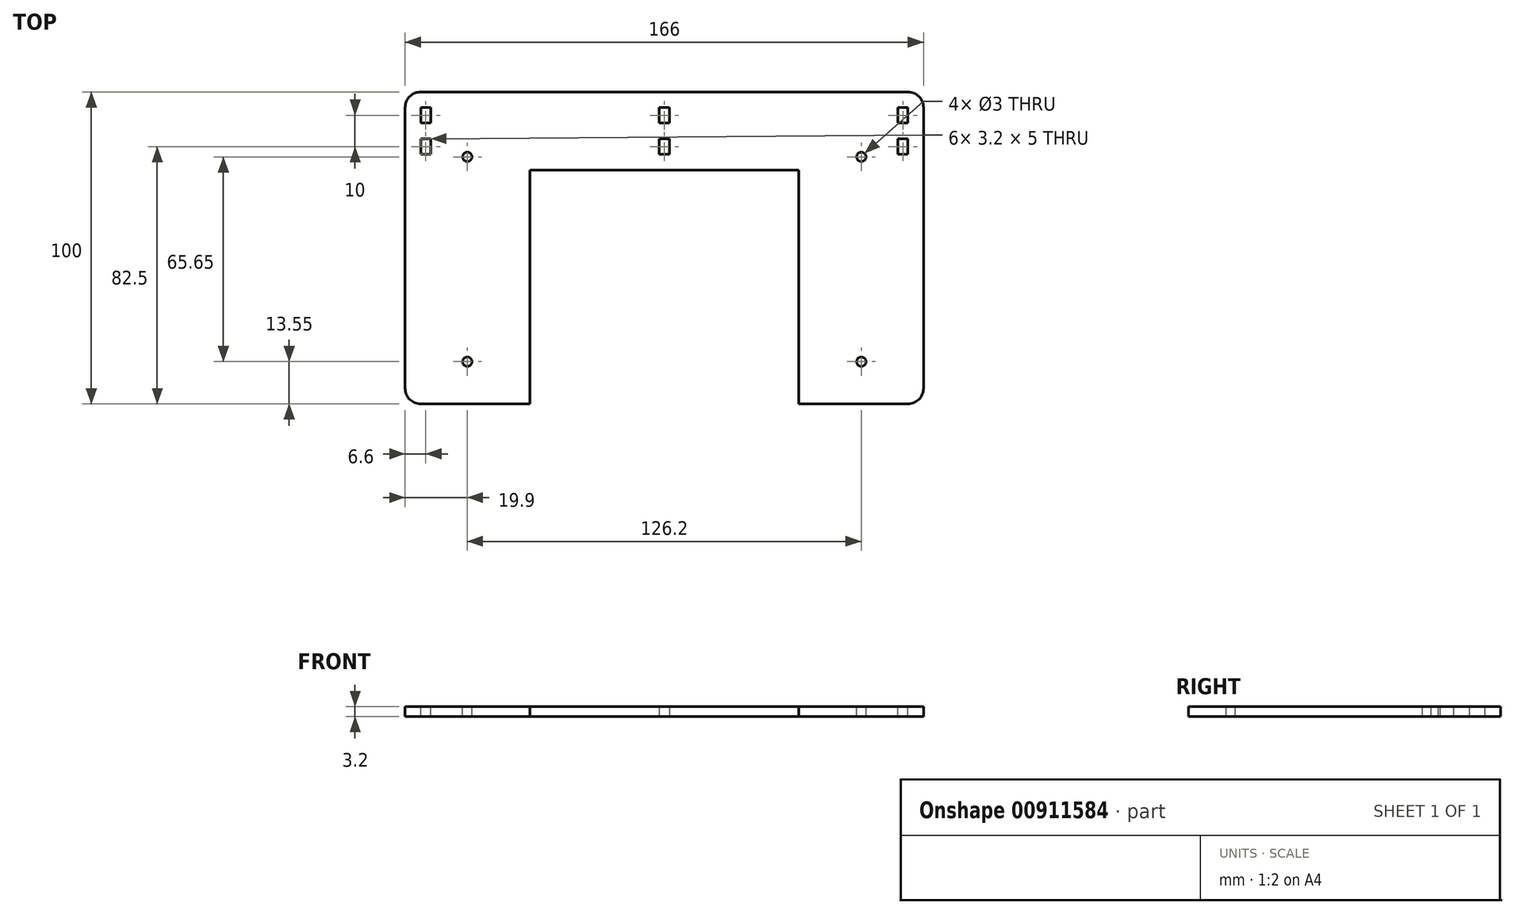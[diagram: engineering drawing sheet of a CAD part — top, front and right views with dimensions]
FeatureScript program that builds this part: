
annotation { "Feature Type Name" : "Feature", "Feature Type Description" : "" }
export const myFeature = defineFeature(function(context is Context, id is Id, definition is map)
    precondition{}
    {
        {
            var Q0;
            Q0=qCreatedBy(makeId("Top.planeOp"),FACE);
            var sketch = newSketch(context, id + "F0", { "sketchPlane" : qUnion([Q0])});
            skLineSegment(sketch, "E0.bottom", {"start": v(83, 50) * mm, "end": v(-83, 50) * mm});
            skLineSegment(sketch, "E0.top", {"start": v(83, -50) * mm, "end": v(-83, -50) * mm});
            skLineSegment(sketch, "E0.left", {"start": v(83, 50) * mm, "end": v(83, -50) * mm});
            skLineSegment(sketch, "E0.right", {"start": v(-83, 50) * mm, "end": v(-83, -50) * mm});
            skPoint(sketch, "E0.middle", {"position": v(0, 0) * mm});
            skSolve(sketch);
        }
        {
            var Q0;
            Q0=makeQuery(id+"F0.imprint","IMPRINT",FACE,{"disambiguationData":[TD([[makeQuery(id+"F0.imprint","IMPRINT",EDGE,{"derivedFrom":sQuery(id+"F0.wireOp",EDGE,"E0.bottom")}),1.0]])]});
            extrude(context, id + "F1", {"entities" : qUnion([Q0]), "depth" : 3.2 * mm, "offsetDistance" : 25 * mm});
        }
        {
            var Q0;
            Q0=makeQuery(id+"F1.opExtrude","SWEPT_EDGE",EDGE,{"disambiguationData":[OSD([sQuery(id+"F0.wireOp",EDGE,"E0.bottom"),sQuery(id+"F0.wireOp",EDGE,"E0.left")])]});
            var Q1;
            Q1=makeQuery(id+"F1.opExtrude","SWEPT_EDGE",EDGE,{"disambiguationData":[OSD([sQuery(id+"F0.wireOp",EDGE,"E0.top"),sQuery(id+"F0.wireOp",EDGE,"E0.left")])]});
            var Q2;
            Q2=makeQuery(id+"F1.opExtrude","SWEPT_EDGE",EDGE,{"disambiguationData":[OSD([sQuery(id+"F0.wireOp",EDGE,"E0.top"),sQuery(id+"F0.wireOp",EDGE,"E0.right")])]});
            var Q3;
            Q3=makeQuery(id+"F1.opExtrude","SWEPT_EDGE",EDGE,{"disambiguationData":[OSD([sQuery(id+"F0.wireOp",EDGE,"E0.bottom"),sQuery(id+"F0.wireOp",EDGE,"E0.right")])]});
            fillet(context, id + "F2", {"entities" : qUnion([Q0, Q1, Q2, Q3]), "radius" : 5 * mm, "tangentPropagation" : true, "allowEdgeOverflow" : false});
        }
        {
            var Q0;
            Q0=makeQuery(id+"F1.opExtrude","CAP_FACE",FACE,{"disambiguationData":[OSD([sQuery(id+"F0.wireOp",EDGE,"E0.bottom"),sQuery(id+"F0.wireOp",EDGE,"E0.top"),sQuery(id+"F0.wireOp",EDGE,"E0.left"),sQuery(id+"F0.wireOp",EDGE,"E0.right")])],"isStart":false});
            var sketch = newSketch(context, id + "F3", { "sketchPlane" : qUnion([Q0])});
            skLineSegment(sketch, "E1", {"start": v(0, 50) * mm, "end": v(0, 29.2) * mm, "construction": true});
            skLineSegment(sketch, "E2", {"start": v(0, 29.2) * mm, "end": v(63.1, 29.2) * mm, "construction": true});
            skCircle(sketch, "E3", {"center": v(63.1, 29.2) * mm, "radius": 1.5 * mm});
            skCircle(sketch, "E4.MirrorC", {"center": v(-63.1, 29.2) * mm, "radius": 1.5 * mm});
            skLineSegment(sketch, "E5", {"start": v(0, 29.2) * mm, "end": v(0, -3.62) * mm, "construction": true});
            skLineSegment(sketch, "E6", {"start": v(0, -3.62) * mm, "end": v(38.49, -3.62) * mm, "construction": true});
            skCircle(sketch, "E7.MirrorC", {"center": v(-63.1, -36.45) * mm, "radius": 1.5 * mm});
            skCircle(sketch, "E8.MirrorC", {"center": v(63.1, -36.45) * mm, "radius": 1.5 * mm});
            skSolve(sketch);
        }
        {
            var Q0;
            Q0 = qSketchRegion(id + "F3", true);
            extrude(context, id + "F4", {"entities" : qUnion([Q0]), "operationType" : NewBodyOperationType.REMOVE, "oppositeDirection" : true, "depth" : 25 * mm, "offsetDistance" : 25 * mm});
        }
        {
            var Q0;
            Q0=makeQuery(id+"F1.opExtrude","CAP_FACE",FACE,{"disambiguationData":[OSD([sQuery(id+"F0.wireOp",EDGE,"E0.bottom"),sQuery(id+"F0.wireOp",EDGE,"E0.top"),sQuery(id+"F0.wireOp",EDGE,"E0.left"),sQuery(id+"F0.wireOp",EDGE,"E0.right")])],"isStart":false});
            var sketch = newSketch(context, id + "F5", { "sketchPlane" : qUnion([Q0])});
            skLineSegment(sketch, "E9", {"start": v(-63.1, -36.45) * mm, "end": v(-63.1, 29.2) * mm, "construction": true});
            skLineSegment(sketch, "E10", {"start": v(-63.1, 29.2) * mm, "end": v(63.1, 29.2) * mm, "construction": true});
            skLineSegment(sketch, "E11", {"start": v(63.1, 29.2) * mm, "end": v(63.1, -50) * mm, "construction": true});
            skLineSegment(sketch, "E12", {"start": v(-63.1, -36.45) * mm, "end": v(-63.1, -50) * mm, "construction": true});
            skLineSegment(sketch, "E13.0", {"start": v(43.1, 9.2) * mm, "end": v(43.1, -50) * mm, "construction": true});
            skLineSegment(sketch, "E13.1", {"start": v(-43.1, 9.2) * mm, "end": v(43.1, 9.2) * mm, "construction": true});
            skLineSegment(sketch, "E13.2", {"start": v(-43.1, -36.45) * mm, "end": v(-43.1, 9.2) * mm, "construction": true});
            skLineSegment(sketch, "E13.3", {"start": v(-43.1, -36.45) * mm, "end": v(-43.1, -50) * mm, "construction": true});
            skLineSegment(sketch, "E14", {"start": v(0, 50) * mm, "end": v(0, 30) * mm});
            skLineSegment(sketch, "E15", {"start": v(-43.1, -50) * mm, "end": v(-43.1, 30) * mm});
            skLineSegment(sketch, "E16", {"start": v(-43.1, 30) * mm, "end": v(0, 30) * mm});
            skLineSegment(sketch, "E17.MirrorCS", {"start": v(43.1, 30) * mm, "end": v(0, 30) * mm});
            skLineSegment(sketch, "E18.MirrorCS", {"start": v(43.1, -50) * mm, "end": v(43.1, 30) * mm});
            skLineSegment(sketch, "E19", {"start": v(-43.1, -50) * mm, "end": v(43.1, -50) * mm});
            skSolve(sketch);
        }
        {
            var Q0;
            Q0=makeQuery(id+"F5.imprint","IMPRINT",FACE,{"disambiguationData":[TD([[makeQuery(id+"F5.imprint","IMPRINT",EDGE,{"derivedFrom":sQuery(id+"F5.wireOp",EDGE,"E15")}),-1.0]])]});
            extrude(context, id + "F6", {"entities" : qUnion([Q0]), "operationType" : NewBodyOperationType.REMOVE, "oppositeDirection" : true, "depth" : 25 * mm, "offsetDistance" : 25 * mm});
        }
        {
            var Q0;
            Q0=makeQuery(id+"F1.opExtrude","CAP_FACE",FACE,{"disambiguationData":[OSD([sQuery(id+"F0.wireOp",EDGE,"E0.bottom"),sQuery(id+"F0.wireOp",EDGE,"E0.top"),sQuery(id+"F0.wireOp",EDGE,"E0.left"),sQuery(id+"F0.wireOp",EDGE,"E0.right")])],"isStart":false});
            var sketch = newSketch(context, id + "F7", { "sketchPlane" : qUnion([Q0])});
            skLineSegment(sketch, "E20", {"start": v(-78, 50) * mm, "end": v(-78, 45) * mm, "construction": true});
            skLineSegment(sketch, "E21", {"start": v(-78, 45) * mm, "end": v(-78, 25) * mm, "construction": true});
            skLineSegment(sketch, "E22.bottom", {"start": v(-78, 45) * mm, "end": v(-74.8, 45) * mm});
            skLineSegment(sketch, "E22.top", {"start": v(-78, 40) * mm, "end": v(-74.8, 40) * mm});
            skLineSegment(sketch, "E22.left", {"start": v(-78, 45) * mm, "end": v(-78, 40) * mm});
            skLineSegment(sketch, "E22.right", {"start": v(-74.8, 45) * mm, "end": v(-74.8, 40) * mm});
            skLineSegment(sketch, "E23", {"start": v(-78, 40) * mm, "end": v(-78, 35) * mm, "construction": true});
            skLineSegment(sketch, "E24.bottom", {"start": v(-78, 35) * mm, "end": v(-74.8, 35) * mm});
            skLineSegment(sketch, "E24.top", {"start": v(-78, 30) * mm, "end": v(-74.8, 30) * mm});
            skLineSegment(sketch, "E24.left", {"start": v(-78, 35) * mm, "end": v(-78, 30) * mm});
            skLineSegment(sketch, "E24.right", {"start": v(-74.8, 35) * mm, "end": v(-74.8, 30) * mm});
            skLineSegment(sketch, "E25", {"start": v(0, 30) * mm, "end": v(0, 37.4) * mm, "construction": true});
            skLineSegment(sketch, "E26.MirrorCS", {"start": v(78, 50) * mm, "end": v(78, 45) * mm, "construction": true});
            skLineSegment(sketch, "E27.MirrorCS", {"start": v(78, 35) * mm, "end": v(74.8, 35) * mm});
            skLineSegment(sketch, "E28.MirrorCS", {"start": v(78, 30) * mm, "end": v(74.8, 30) * mm});
            skLineSegment(sketch, "E29.MirrorCS", {"start": v(78, 45) * mm, "end": v(74.8, 45) * mm});
            skLineSegment(sketch, "E30.MirrorCS", {"start": v(78, 40) * mm, "end": v(74.8, 40) * mm});
            skLineSegment(sketch, "E31.MirrorCS", {"start": v(78, 45) * mm, "end": v(78, 40) * mm});
            skLineSegment(sketch, "E32.MirrorCS", {"start": v(78, 40) * mm, "end": v(78, 35) * mm, "construction": true});
            skLineSegment(sketch, "E33.MirrorCS", {"start": v(78, 35) * mm, "end": v(78, 30) * mm});
            skLineSegment(sketch, "E34.MirrorCS", {"start": v(74.8, 45) * mm, "end": v(74.8, 40) * mm});
            skLineSegment(sketch, "E35.MirrorCS", {"start": v(74.8, 35) * mm, "end": v(74.8, 30) * mm});
            skLineSegment(sketch, "E36.MirrorCS", {"start": v(78, 45) * mm, "end": v(78, 25) * mm, "construction": true});
            skSolve(sketch);
        }
        {
            var Q0;
            Q0 = qSketchRegion(id + "F7", true);
            extrude(context, id + "F8", {"entities" : qUnion([Q0]), "operationType" : NewBodyOperationType.REMOVE, "oppositeDirection" : true, "depth" : 25 * mm, "offsetDistance" : 25 * mm});
        }
        {
            var Q0;
            Q0=makeQuery(id+"F1.opExtrude","CAP_FACE",FACE,{"disambiguationData":[OSD([sQuery(id+"F0.wireOp",EDGE,"E0.bottom"),sQuery(id+"F0.wireOp",EDGE,"E0.top"),sQuery(id+"F0.wireOp",EDGE,"E0.left"),sQuery(id+"F0.wireOp",EDGE,"E0.right")])],"isStart":false});
            var sketch = newSketch(context, id + "F9", { "sketchPlane" : qUnion([Q0])});
            skLineSegment(sketch, "E37", {"start": v(-78, 30) * mm, "end": v(-78, 25) * mm, "construction": true});
            skLineSegment(sketch, "E38", {"start": v(-78, 25) * mm, "end": v(43.1, 25) * mm, "construction": true});
            skLineSegment(sketch, "E39.bottom", {"start": v(43.1, 25) * mm, "end": v(-43.1, 25) * mm});
            skLineSegment(sketch, "E39.top", {"start": v(43.1, 30) * mm, "end": v(-43.1, 30) * mm});
            skLineSegment(sketch, "E39.left", {"start": v(43.1, 25) * mm, "end": v(43.1, 30) * mm});
            skLineSegment(sketch, "E39.right", {"start": v(-43.1, 25) * mm, "end": v(-43.1, 30) * mm});
            skSolve(sketch);
        }
        {
            var Q0;
            Q0 = qSketchRegion(id + "F9", true);
            var Q1;
            Q1=makeQuery(id+"F1.opExtrude","CAP_FACE",FACE,{"disambiguationData":[OSD([sQuery(id+"F0.wireOp",EDGE,"E0.bottom"),sQuery(id+"F0.wireOp",EDGE,"E0.top"),sQuery(id+"F0.wireOp",EDGE,"E0.left"),sQuery(id+"F0.wireOp",EDGE,"E0.right")])],"isStart":true});
            extrude(context, id + "F10", {"entities" : qUnion([Q0]), "operationType" : NewBodyOperationType.ADD, "endBound" : BoundingType.UP_TO_SURFACE, "oppositeDirection" : true, "depth" : 25 * mm, "endBoundEntityFace" : qUnion([Q1]), "offsetDistance" : 25 * mm});
        }
        {
            var Q0;
            Q0=makeQuery(id+"F10.boolean.opBoolean","MERGE",FACE,{"derivedFrom":[makeQuery(id+"F1.opExtrude","CAP_FACE",FACE,{"disambiguationData":[OSD([sQuery(id+"F0.wireOp",EDGE,"E0.bottom"),sQuery(id+"F0.wireOp",EDGE,"E0.top"),sQuery(id+"F0.wireOp",EDGE,"E0.left"),sQuery(id+"F0.wireOp",EDGE,"E0.right")])],"isStart":true}),makeQuery(id+"F10.opExtrude","CAP_FACE",FACE,{"disambiguationData":[OSD([sQuery(id+"F9.wireOp",EDGE,"E39.bottom"),sQuery(id+"F9.wireOp",EDGE,"E39.top"),sQuery(id+"F9.wireOp",EDGE,"E39.left"),sQuery(id+"F9.wireOp",EDGE,"E39.right")])],"isStart":false})]});
            var sketch = newSketch(context, id + "F11", { "sketchPlane" : qUnion([Q0])});
            skLineSegment(sketch, "E40", {"start": v(-74.8, -30) * mm, "end": v(0, -30) * mm, "construction": true});
            skLineSegment(sketch, "E41", {"start": v(0, -30) * mm, "end": v(0, -35) * mm, "construction": true});
            skLineSegment(sketch, "E42.bottom", {"start": v(1.6, -30) * mm, "end": v(-1.6, -30) * mm});
            skLineSegment(sketch, "E42.top", {"start": v(1.6, -35) * mm, "end": v(-1.6, -35) * mm});
            skLineSegment(sketch, "E42.left", {"start": v(1.6, -30) * mm, "end": v(1.6, -35) * mm});
            skLineSegment(sketch, "E42.right", {"start": v(-1.6, -30) * mm, "end": v(-1.6, -35) * mm});
            skPoint(sketch, "E42.middle", {"position": v(0, -32.5) * mm});
            skLineSegment(sketch, "E43", {"start": v(-1.6, -35) * mm, "end": v(-1.6, -40) * mm, "construction": true});
            skLineSegment(sketch, "E44.bottom", {"start": v(-1.6, -40) * mm, "end": v(1.6, -40) * mm});
            skLineSegment(sketch, "E44.top", {"start": v(-1.6, -45) * mm, "end": v(1.6, -45) * mm});
            skLineSegment(sketch, "E44.left", {"start": v(-1.6, -40) * mm, "end": v(-1.6, -45) * mm});
            skLineSegment(sketch, "E44.right", {"start": v(1.6, -40) * mm, "end": v(1.6, -45) * mm});
            skSolve(sketch);
        }
        {
            var Q0;
            Q0 = qSketchRegion(id + "F11", true);
            extrude(context, id + "F12", {"entities" : qUnion([Q0]), "operationType" : NewBodyOperationType.REMOVE, "oppositeDirection" : true, "depth" : 25 * mm, "offsetDistance" : 25 * mm});
        }
    });
